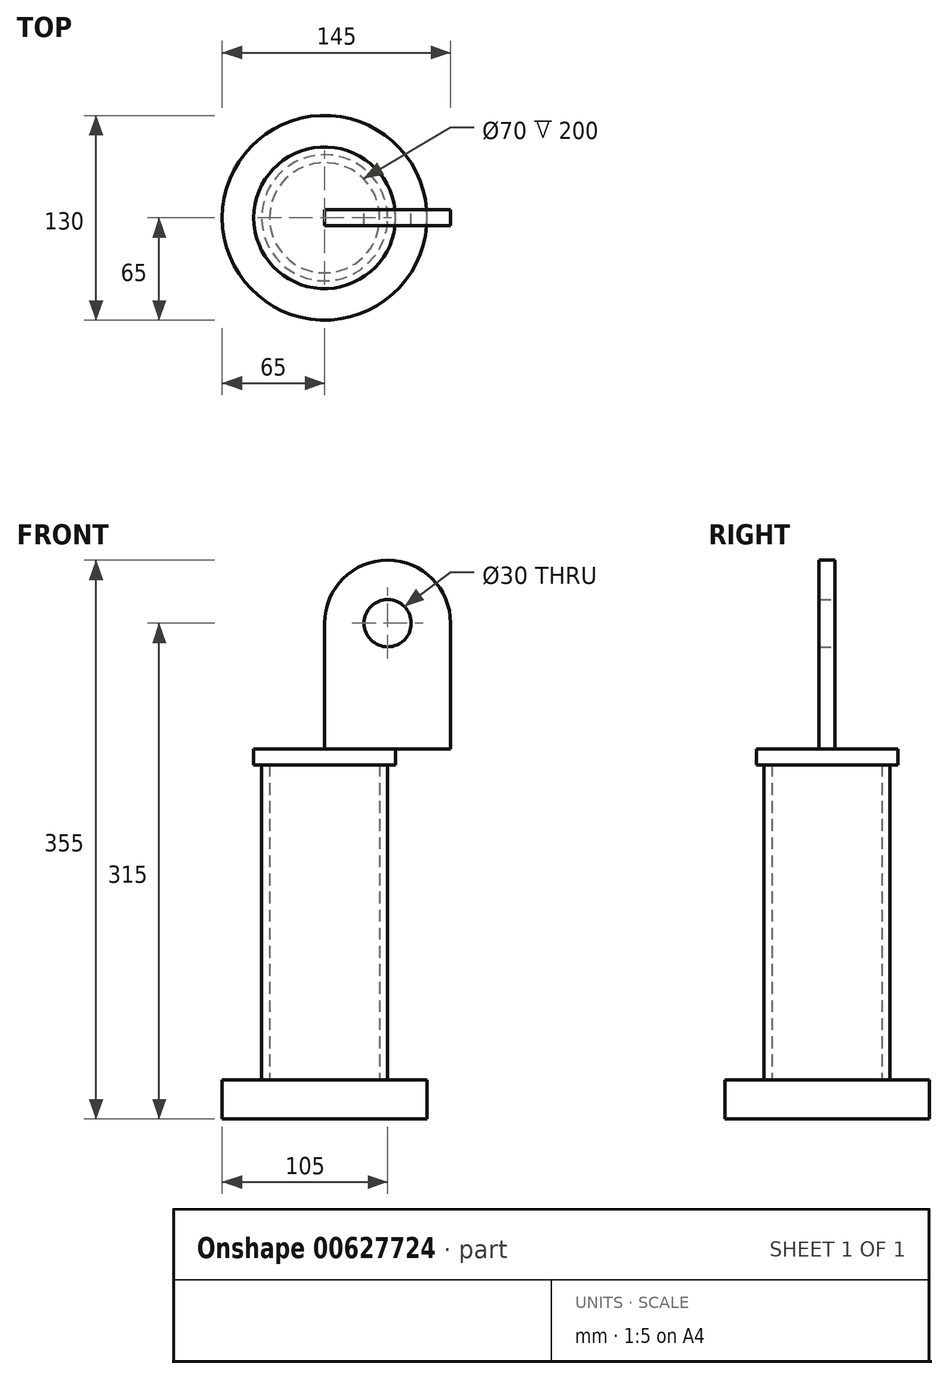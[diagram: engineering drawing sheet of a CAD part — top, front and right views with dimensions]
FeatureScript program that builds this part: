
annotation { "Feature Type Name" : "Feature", "Feature Type Description" : "" }
export const myFeature = defineFeature(function(context is Context, id is Id, definition is map)
    precondition{}
    {
        {
            var Q0;
            Q0=qCreatedBy(makeId("Top.planeOp"),FACE);
            var sketch = newSketch(context, id + "F0", { "sketchPlane" : qUnion([Q0])});
            skCircle(sketch, "E0", {"center": v(0, 0) * mm, "radius": 65 * mm});
            skSolve(sketch);
        }
        {
            var Q0;
            Q0=makeQuery(id+"F0.imprint","IMPRINT",FACE,{"disambiguationData":[TD([[makeQuery(id+"F0.imprint","IMPRINT",EDGE,{"derivedFrom":sQuery(id+"F0.wireOp",EDGE,"E0")}),1.0]])]});
            extrude(context, id + "F1", {"entities" : qUnion([Q0]), "depth" : 25 * mm, "offsetDistance" : 25 * mm});
        }
        {
            var Q0;
            Q0=makeQuery(id+"F1.opExtrude","CAP_FACE",FACE,{"disambiguationData":[OSD([sQuery(id+"F0.wireOp",EDGE,"E0")])],"isStart":false});
            var sketch = newSketch(context, id + "F2", { "sketchPlane" : qUnion([Q0])});
            skCircle(sketch, "E1", {"center": v(0, 0) * mm, "radius": 40 * mm});
            skCircle(sketch, "E2", {"center": v(0, 0) * mm, "radius": 35 * mm});
            skSolve(sketch);
        }
        {
            var Q0;
            Q0 = qSketchRegion(id + "F2", true);
            extrude(context, id + "F3", {"entities" : qUnion([Q0]), "depth" : 200 * mm, "offsetDistance" : 25 * mm});
        }
        {
            var Q0;
            Q0=makeQuery(id+"F3.opExtrude","CAP_FACE",FACE,{"disambiguationData":[OSD([sQuery(id+"F2.wireOp",EDGE,"E1"),sQuery(id+"F2.wireOp",EDGE,"E2")])],"isStart":false});
            var sketch = newSketch(context, id + "F4", { "sketchPlane" : qUnion([Q0])});
            skCircle(sketch, "E3", {"center": v(0, 0) * mm, "radius": 45 * mm});
            skSolve(sketch);
        }
        {
            var Q0;
            Q0 = qSketchRegion(id + "F4", true);
            extrude(context, id + "F5", {"entities" : qUnion([Q0]), "operationType" : NewBodyOperationType.ADD, "depth" : 10 * mm, "offsetDistance" : 25 * mm});
        }
        {
            var Q0;
            Q0=qCreatedBy(makeId("Front.planeOp"),FACE);
            var sketch = newSketch(context, id + "F6", { "sketchPlane" : qUnion([Q0])});
            skLineSegment(sketch, "E4.bottom", {"start": v(0, 235) * mm, "end": v(80, 235) * mm});
            skLineSegment(sketch, "E4.left", {"start": v(0, 235) * mm, "end": v(0, 315) * mm});
            skLineSegment(sketch, "E4.right", {"start": v(80, 235) * mm, "end": v(80, 315) * mm});
            skArc(sketch, "E5", {"start": v(80, 315) * mm, "mid": v(40, 355) * mm, "end": v(0, 315) * mm});
            skCircle(sketch, "E6", {"center": v(40, 315) * mm, "radius": 15 * mm});
            skSolve(sketch);
        }
        {
            var Q0;
            Q0 = qSketchRegion(id + "F6", true);
            extrude(context, id + "F7", {"entities" : qUnion([Q0]), "depth" : 5 * mm, "offsetDistance" : 25 * mm, "hasSecondDirection" : true, "secondDirectionOppositeDirection" : true, "secondDirectionDepth" : 5 * mm});
        }
    });
